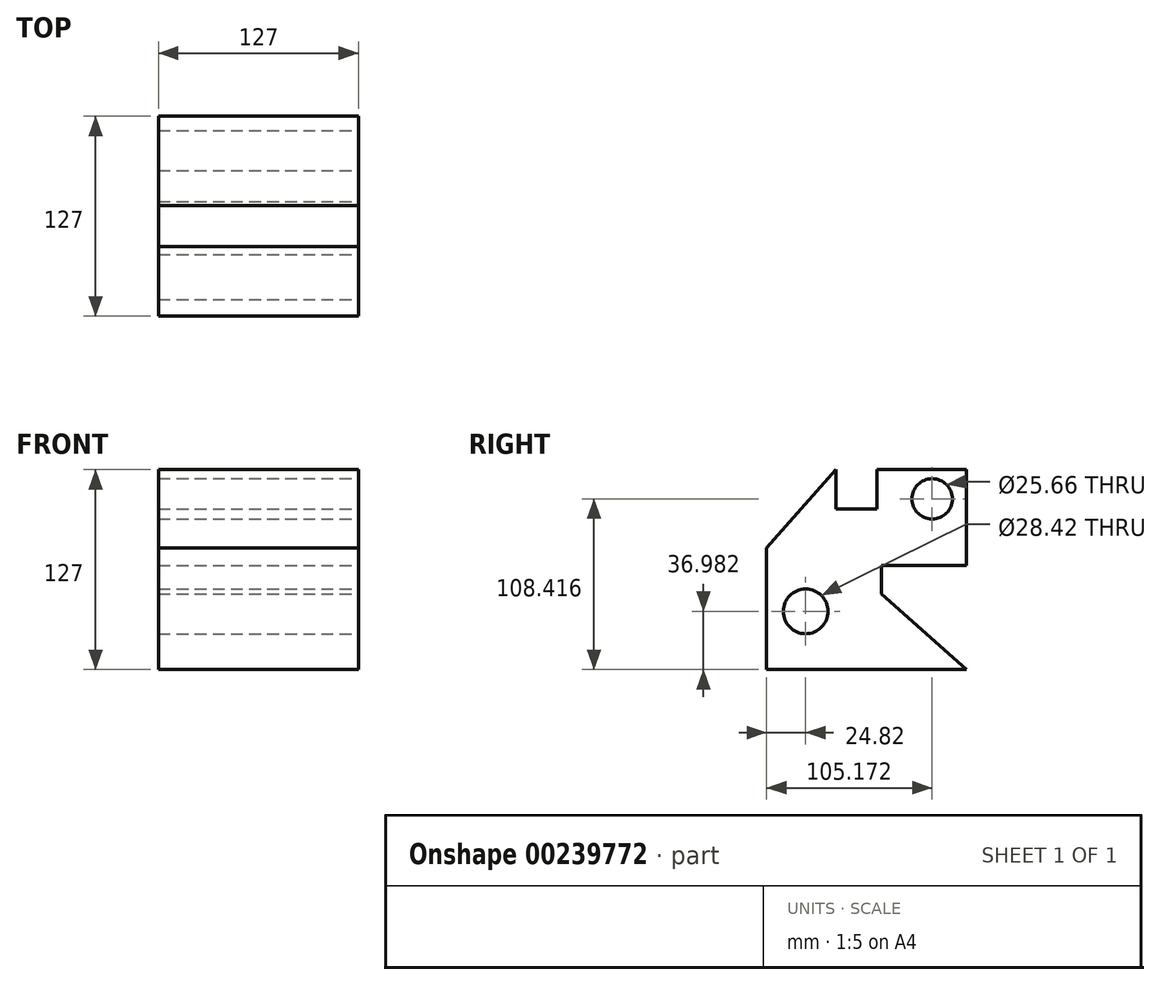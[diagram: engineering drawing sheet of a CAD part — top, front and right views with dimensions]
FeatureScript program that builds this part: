
annotation { "Feature Type Name" : "Feature", "Feature Type Description" : "" }
export const myFeature = defineFeature(function(context is Context, id is Id, definition is map)
    precondition{}
    {
        {
            var Q0;
            Q0=qCreatedBy(makeId("Front.planeOp"),FACE);
            var sketch = newSketch(context, id + "F0", { "sketchPlane" : qUnion([Q0])});
            skLineSegment(sketch, "E0.bottom", {"start": v(-98.33, 60.84) * mm, "end": v(28.67, 60.84) * mm});
            skLineSegment(sketch, "E0.top", {"start": v(-98.33, -66.16) * mm, "end": v(28.67, -66.16) * mm});
            skLineSegment(sketch, "E0.left", {"start": v(-98.33, 60.84) * mm, "end": v(-98.33, -66.16) * mm});
            skLineSegment(sketch, "E0.right", {"start": v(28.67, 60.84) * mm, "end": v(28.67, -66.16) * mm});
            skSolve(sketch);
        }
        {
            var Q0;
            Q0=makeQuery(id+"F0.imprint","IMPRINT",FACE,{"disambiguationData":[TD([[makeQuery(id+"F0.imprint","IMPRINT",EDGE,{"derivedFrom":sQuery(id+"F0.wireOp",EDGE,"E0.bottom")}),-1.0]])]});
            extrude(context, id + "F1", {"entities" : qUnion([Q0]), "depth" : 127 * mm});
        }
        {
            var Q0;
            Q0=makeQuery(id+"F1.opExtrude","SWEPT_FACE",FACE,{"disambiguationData":[OSD([sQuery(id+"F0.wireOp",EDGE,"E0.right")])]});
            var sketch = newSketch(context, id + "F2", { "sketchPlane" : qUnion([Q0])});
            skLineSegment(sketch, "E1.bottom", {"start": v(-82.87, 60.84) * mm, "end": v(-56.79, 60.84) * mm});
            skLineSegment(sketch, "E1.top", {"start": v(-82.87, 35.79) * mm, "end": v(-56.79, 35.79) * mm});
            skLineSegment(sketch, "E1.left", {"start": v(-82.87, 60.84) * mm, "end": v(-82.87, 35.79) * mm});
            skLineSegment(sketch, "E1.right", {"start": v(-56.79, 60.84) * mm, "end": v(-56.79, 35.79) * mm});
            skSolve(sketch);
        }
        {
            var Q0;
            Q0=makeQuery(id+"F2.imprint","IMPRINT",FACE,{"disambiguationData":[TD([[makeQuery(id+"F2.imprint","IMPRINT",EDGE,{"derivedFrom":sQuery(id+"F2.wireOp",EDGE,"E1.bottom")}),-1.0]])]});
            extrude(context, id + "F3", {"entities" : qUnion([Q0]), "operationType" : NewBodyOperationType.REMOVE, "endBound" : BoundingType.THROUGH_ALL, "oppositeDirection" : true, "depth" : 25.4 * mm});
        }
        {
            var Q0;
            Q0=makeQuery(id+"F1.opExtrude","SWEPT_FACE",FACE,{"disambiguationData":[OSD([sQuery(id+"F0.wireOp",EDGE,"E0.right")])]});
            var sketch = newSketch(context, id + "F4", { "sketchPlane" : qUnion([Q0])});
            skLineSegment(sketch, "E2", {"start": v(-82.87, 60.84) * mm, "end": v(-127, 11.03) * mm});
            skSolve(sketch);
        }
        {
            var Q0;
            {var subQ0=sQuery(id+"F4.wireOp",EDGE,"E2");Q0=makeQuery(id+"F4.imprint","IMPRINT",FACE,{"disambiguationData":[TD([[makeQuery(id+"F4.imprint","IMPRINT",EDGE,{"derivedFrom":subQ0}),-1.0]])]});}
            extrude(context, id + "F5", {"entities" : qUnion([Q0]), "operationType" : NewBodyOperationType.REMOVE, "endBound" : BoundingType.THROUGH_ALL, "oppositeDirection" : true, "depth" : 25.4 * mm});
        }
        {
            var Q0;
            Q0=makeQuery(id+"F1.opExtrude","SWEPT_FACE",FACE,{"disambiguationData":[OSD([sQuery(id+"F0.wireOp",EDGE,"E0.right")])]});
            var sketch = newSketch(context, id + "F6", { "sketchPlane" : qUnion([Q0])});
            skCircle(sketch, "E3", {"center": v(-21.83, 42.26) * mm, "radius": 12.83 * mm});
            skSolve(sketch);
        }
        {
            var Q0;
            Q0=makeQuery(id+"F6.imprint","IMPRINT",FACE,{"disambiguationData":[TD([[makeQuery(id+"F6.imprint","IMPRINT",EDGE,{"derivedFrom":sQuery(id+"F6.wireOp",EDGE,"E3")}),1.0]])]});
            extrude(context, id + "F7", {"entities" : qUnion([Q0]), "operationType" : NewBodyOperationType.REMOVE, "endBound" : BoundingType.THROUGH_ALL, "oppositeDirection" : true, "depth" : 25.4 * mm});
        }
        {
            var Q0;
            Q0=makeQuery(id+"F1.opExtrude","SWEPT_FACE",FACE,{"disambiguationData":[OSD([sQuery(id+"F0.wireOp",EDGE,"E0.right")])]});
            var sketch = newSketch(context, id + "F8", { "sketchPlane" : qUnion([Q0])});
            skCircle(sketch, "E4", {"center": v(-102.18, -29.18) * mm, "radius": 14.2 * mm});
            skSolve(sketch);
        }
        {
            var Q0;
            Q0=makeQuery(id+"F8.imprint","IMPRINT",FACE,{"disambiguationData":[TD([[makeQuery(id+"F8.imprint","IMPRINT",EDGE,{"derivedFrom":sQuery(id+"F8.wireOp",EDGE,"E4")}),1.0]])]});
            extrude(context, id + "F9", {"entities" : qUnion([Q0]), "operationType" : NewBodyOperationType.REMOVE, "endBound" : BoundingType.THROUGH_ALL, "oppositeDirection" : true, "depth" : 25.4 * mm});
        }
        {
            var Q0;
            Q0=makeQuery(id+"F1.opExtrude","SWEPT_FACE",FACE,{"disambiguationData":[OSD([sQuery(id+"F0.wireOp",EDGE,"E0.right")])]});
            var sketch = newSketch(context, id + "F10", { "sketchPlane" : qUnion([Q0])});
            skLineSegment(sketch, "E5", {"start": v(0, 0) * mm, "end": v(-54.05, 0) * mm});
            skLineSegment(sketch, "E6", {"start": v(-54.05, 0) * mm, "end": v(-54.05, -18.06) * mm});
            skLineSegment(sketch, "E7", {"start": v(-54.05, -18.06) * mm, "end": v(0, -66.16) * mm});
            skSolve(sketch);
        }
        {
            var Q0;
            {var subQ0=sQuery(id+"F10.wireOp",EDGE,"E5");Q0=makeQuery(id+"F10.imprint","IMPRINT",FACE,{"disambiguationData":[TD([[makeQuery(id+"F10.imprint","IMPRINT",EDGE,{"derivedFrom":subQ0}),1.0]])]});}
            extrude(context, id + "F11", {"entities" : qUnion([Q0]), "operationType" : NewBodyOperationType.REMOVE, "endBound" : BoundingType.THROUGH_ALL, "oppositeDirection" : true, "depth" : 25.4 * mm});
        }
    });
